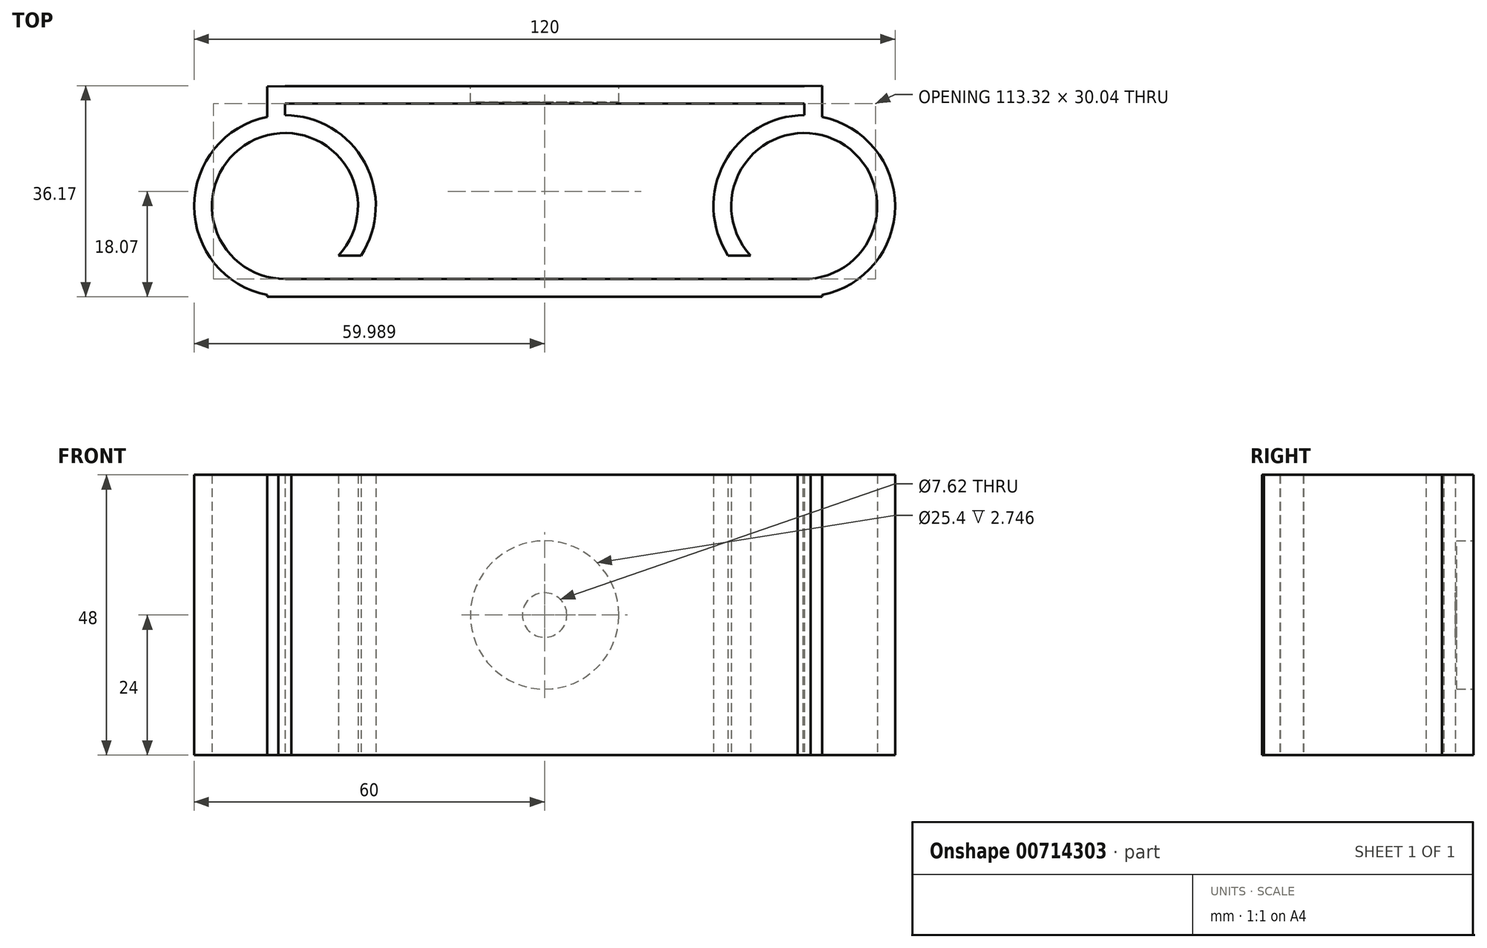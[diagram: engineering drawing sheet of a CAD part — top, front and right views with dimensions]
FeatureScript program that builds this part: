
annotation { "Feature Type Name" : "Feature", "Feature Type Description" : "" }
export const myFeature = defineFeature(function(context is Context, id is Id, definition is map)
    precondition{}
    {
        {
            var Q0;
            Q0=qCreatedBy(makeId("Top.planeOp"),FACE);
            var sketch = newSketch(context, id + "F0", { "sketchPlane" : qUnion([Q0])});
            skLineSegment(sketch, "E0.bottom", {"start": v(-44.45, 15) * mm, "end": v(44.45, 15) * mm});
            skLineSegment(sketch, "E0.top", {"start": v(-44.45, -15) * mm, "end": v(44.45, -15) * mm});
            skLineSegment(sketch, "E0.left", {"start": v(-44.45, 15) * mm, "end": v(-44.45, -15) * mm});
            skLineSegment(sketch, "E0.right", {"start": v(44.45, 15) * mm, "end": v(44.45, -15) * mm});
            skPoint(sketch, "E0.middle", {"position": v(0, 0) * mm});
            skLineSegment(sketch, "E1.bottom", {"start": v(44.45, 15) * mm, "end": v(-44.45, 15) * mm});
            skLineSegment(sketch, "E1.top", {"start": v(44.45, 18) * mm, "end": v(-44.45, 18) * mm});
            skLineSegment(sketch, "E1.left", {"start": v(44.45, 15) * mm, "end": v(44.45, 18) * mm});
            skLineSegment(sketch, "E1.right", {"start": v(-44.45, 15) * mm, "end": v(-44.45, 18) * mm});
            skPoint(sketch, "E1.middle", {"position": v(0, 16.5) * mm});
            skLineSegment(sketch, "E2.0", {"start": v(-47.5, 17.94) * mm, "end": v(-47.5, -18.05) * mm});
            skLineSegment(sketch, "E2.1", {"start": v(-47.5, -18.05) * mm, "end": v(47.5, -18.05) * mm});
            skLineSegment(sketch, "E2.2", {"start": v(47.5, 18.08) * mm, "end": v(47.5, -18.05) * mm});
            skPoint(sketch, "E3", {"position": v(44.45, 0) * mm});
            skPoint(sketch, "E4", {"position": v(-44.45, 0) * mm});
            skArc(sketch, "E5", {"start": v(44.57, -15.04) * mm, "mid": v(49.4, 8.94) * mm, "end": v(35.28, -11.04) * mm});
            skArc(sketch, "E6", {"start": v(43.45, -15) * mm, "mid": v(44, -15.03) * mm, "end": v(44.57, -15.04) * mm});
            skLineSegment(sketch, "E7", {"start": v(-47.5, 17.94) * mm, "end": v(-44.45, 18) * mm});
            skLineSegment(sketch, "E8", {"start": v(44.45, 18) * mm, "end": v(47.5, 18.08) * mm});
            skArc(sketch, "E9", {"start": v(35.15, -15) * mm, "mid": v(55.8, 8.09) * mm, "end": v(31.4, -11) * mm});
            skLineSegment(sketch, "E10", {"start": v(35.28, -11.04) * mm, "end": v(31.4, -11) * mm});
            skLineSegment(sketch, "E11", {"start": v(44.57, -15.04) * mm, "end": v(35.15, -15) * mm});
            skArc(sketch, "E12", {"start": v(-44.43, -15.04) * mm, "mid": v(-43.94, -15.03) * mm, "end": v(-43.45, -15) * mm});
            skArc(sketch, "E13", {"start": v(-35.28, -11.04) * mm, "mid": v(-49.46, 8.91) * mm, "end": v(-44.43, -15.04) * mm});
            skArc(sketch, "E14", {"start": v(-31.4, -11) * mm, "mid": v(-55.8, 8.09) * mm, "end": v(-35.15, -15) * mm});
            skLineSegment(sketch, "E15", {"start": v(-35.28, -11.04) * mm, "end": v(-31.4, -11) * mm});
            skLineSegment(sketch, "E16", {"start": v(-35.15, -15) * mm, "end": v(-44.43, -15.04) * mm});
            skSolve(sketch);
        }
        {
            var Q0;
            Q0 = qSketchRegion(id + "F0", true);
            var Q1;
            {var subQ5=sQuery(id+"F0.wireOp",EDGE,"E10");Q1=makeQuery(id+"F0.imprint","IMPRINT",FACE,{"disambiguationData":[TD([[makeQuery(id+"F0.imprint","IMPRINT",EDGE,{"derivedFrom":subQ5}),-1.0]])]});}
            var Q2;
            {var subQ5=sQuery(id+"F0.wireOp",EDGE,"E15");Q2=makeQuery(id+"F0.imprint","IMPRINT",FACE,{"disambiguationData":[TD([[makeQuery(id+"F0.imprint","IMPRINT",EDGE,{"derivedFrom":subQ5}),1.0]])]});}
            extrude(context, id + "F1", {"entities" : qUnion([Q0, Q1, Q2]), "endBound" : BoundingType.SYMMETRIC, "depth" : 48 * mm, "offsetDistance" : 25.4 * mm});
        }
        {
            var Q0;
            Q0=qCreatedBy(makeId("Front.planeOp"),FACE);
            cPlane(context, id + "F2", {"entities" : qUnion([Q0]), "cplaneType" : CPlaneType.OFFSET, "offset" : 18.05 * mm, "oppositeDirection" : true, "width" : 152.4 * mm, "height" : 152.4 * mm});
        }
        {
            var Q0;
            Q0=qCreatedBy(id+"F2.planeOp",FACE);
            var sketch = newSketch(context, id + "F3", { "sketchPlane" : qUnion([Q0])});
            skCircle(sketch, "E17", {"center": v(0, 0) * mm, "radius": 3.81 * mm});
            skSolve(sketch);
        }
        {
            var Q0;
            Q0=qCreatedBy(id+"F2.planeOp",FACE);
            var sketch = newSketch(context, id + "F4", { "sketchPlane" : qUnion([Q0])});
            skCircle(sketch, "E18", {"center": v(0, 0) * mm, "radius": 12.7 * mm});
            skSolve(sketch);
        }
        {
            var Q0;
            Q0 = qSketchRegion(id + "F3", true);
            extrude(context, id + "F5", {"entities" : qUnion([Q0]), "operationType" : NewBodyOperationType.REMOVE, "depth" : 3.05 * mm, "offsetDistance" : 25.4 * mm});
        }
        {
            var Q0;
            Q0 = qSketchRegion(id + "F4", true);
            extrude(context, id + "F6", {"entities" : qUnion([Q0]), "operationType" : NewBodyOperationType.REMOVE, "depth" : 2.8 * mm, "offsetDistance" : 25.4 * mm});
        }
    });
